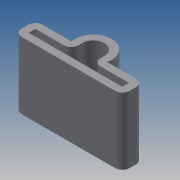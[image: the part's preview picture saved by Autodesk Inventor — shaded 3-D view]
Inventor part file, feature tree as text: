
AUTODESK INVENTOR PART (.ipt)
format: ipt  version: 2013 (Build 170138000, 138)  size: 102,400 bytes
history: native  units: mm
features: extrude x1, fillet x1, sketch x1
ambient origin geometry x8: Origin, YZ Plane, XZ Plane, XY Plane, X Axis, Y Axis, Z Axis, Center Point
bodies: Solid1 (feature_tree)
feature tree (3):
  extrude  "Extrusion1"  Depth=21.0mm
  fillet  "Fillet1"  Radius=5.0mm
  sketch  "Sketch1"  dims[d0=1.5mm d2=21.0mm d3=5.0mm d4=1.6mm d5=1.6mm d6=1.6mm d7=1.6mm d8=15.0mm d9=0.0mm d10=1.6mm]
